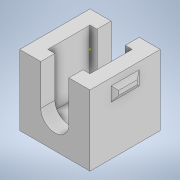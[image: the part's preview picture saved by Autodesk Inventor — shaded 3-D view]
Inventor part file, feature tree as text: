
AUTODESK INVENTOR PART (.ipt)
format: ipt  version: 2022 (Build 260153000, 153)  size: 139,264 bytes
history: native  units: in
note: dims shown in document units (in); Inventor stores cm internally (conversion verified against a paired STEP export)
features: sketch x9, extrude x4, shell x1
ambient origin geometry x8: Origin, YZ Plane, XZ Plane, XY Plane, X Axis, Y Axis, Z Axis, Center Point
bodies: Solid1 (feature_tree)
feature tree (14):
  extrude  "Extrusion1"  Depth=0.1969in
  shell  "Shell1"  Thickness=0.1969in
  extrude  "Extrusion3"  TaperAngle=0.0deg  [1 undecoded]
  sketch  "Sketch4"  dims[d10=0.0394in d11=0.0079in d12=-0.4123in]
  sketch  "Sketch5"  dims[d13=0.0394in d14=0.0787in]
  sketch  "Sketch6"  dims[d15=0.0394in]
  sketch  "Sketch7"  dims[d16=0.0787in]
  sketch  "Sketch8"  dims[d17=0.0394in]
  extrude  "Extrusion4"  Depth=0.0079in
  extrude  "Extrusion5"  Depth=0.0394in
  sketch  "Sketch1"  dims[d0=0.1969in d1=0.1969in d2=0.1969in d3=0.0in]
  sketch  "Sketch3"  dims[d4=0.0394in d8=0.0in d9=0.0in]
  sketch  "Sketch9"  dims[d18=0.0079in d19=-0.4123in]
  sketch  "Sketch10"
note: 1 required parameter value undecoded (feature->parameter linkage not recoverable at this tier; creation-order binding heuristic only, values carry confidence <= 0.55)
